# Revit family: Domotics-DomesticRanges-GEWISS-CHORUS_DATA-SOCKET-OUTLET_RJ11
name_source: partatom
category: Apparecchi elettrici
revit_build: Autodesk Revit 2016 (Build: 20161004_0715(x64)
units: mm (PartAtom-declared; Revit-internal decimal feet)

## family parameters
Condiviso = Sì
Host = Superficie
Mantenere orientamento annotazione = Sì
Numero OmniClass = 23.80.50.14
Punto di calcolo locali = Sì
Quota connettore circolare = Usa diametro
Taglio con vuoti quando caricato = Sì
Tipo di parte = Normale
Titolo OmniClass = Plug Connectors

## types (6) — shared parameters
Carico apparente = 0 VA
Catalogue = DOMOTICS
Catalogue Range = CHORUS - DOMESTIC RANGE
Category = Telephone socket-outlet
Description. = Telephone socket-outlet
Description: = RJ11
Electrocod = 3720
IDF = bb8e3a72-2a5c-4532-8acd-c40bef2c28fa
IDT = 45381b81-222b-4d35-9f73-019257e71c9e
Immagine tipo = GW14402.jpg
Larghezza presa = 23 mm  [stored 0.0754593 ft]
N. poli = 1
No. Chorus modules = 1
No. Chorus modules: = 1
Produttore = GEWISS S.p.A.
Prospetto di default = 1219 mm
SEO = Socket outlet
Simbolo_ = SIMBOLO PRESE TELEFONO : PRESA TEL
Technical sheet = https://www.gewiss.com
Tipo_ = CHORUS PRESE RJ11_BASE : TITANIO
URL = https://www.gewiss.com
Version file RFA = 19.0
Volt = 230 V

## per-type parameters (varying)
| type | Colour | Connection | Descrizione | EAN code | Modello | Type | Type: |
| GW12401 - Black | Black | Screw-on terminals | TELEPHONE CONNECTOR RJ11 1M BLACK | 8011564269033 | GW12401 |  |  |
| GW12402 - Black | Black | Impact tool | TELEPHONE CONNECTOR RJ11 IN-OUT 1M BLACK | 8011564269040 | GW12402 | In out | In out |
| GW14402 - Titanium | Titanium | Impact tool | TELEPHONE CONN. RJ11 IN-OUT 1M TITANIUM | 8011564267091 | GW14402 | In out | In out |
| GW10402 - White | White | Impact tool | TELEPHONE CONNECTOR RJ11 IN-OUT 1M WHITE | 8011564257658 | GW10402 | In out | In out |
| GW14401 - Titanium | Titanium | Screw-on terminals | TELEPHONE CONNECTOR RJ11 1M TITANIUM | 8011564267084 | GW14401 |  |  |
| GW10401 - White | White | Screw-on terminals | TELEPHONE CONNECTOR RJ11 1M WHITE | 8011564257641 | GW10401 |  |  |

note: [stored X ft] marks values corroborated as IEEE doubles in the binary element streams (Revit-internal decimal feet)

## geometry (parser evidence)
native form markers: Sweep x1
no freeform markers — native parametric forms only
